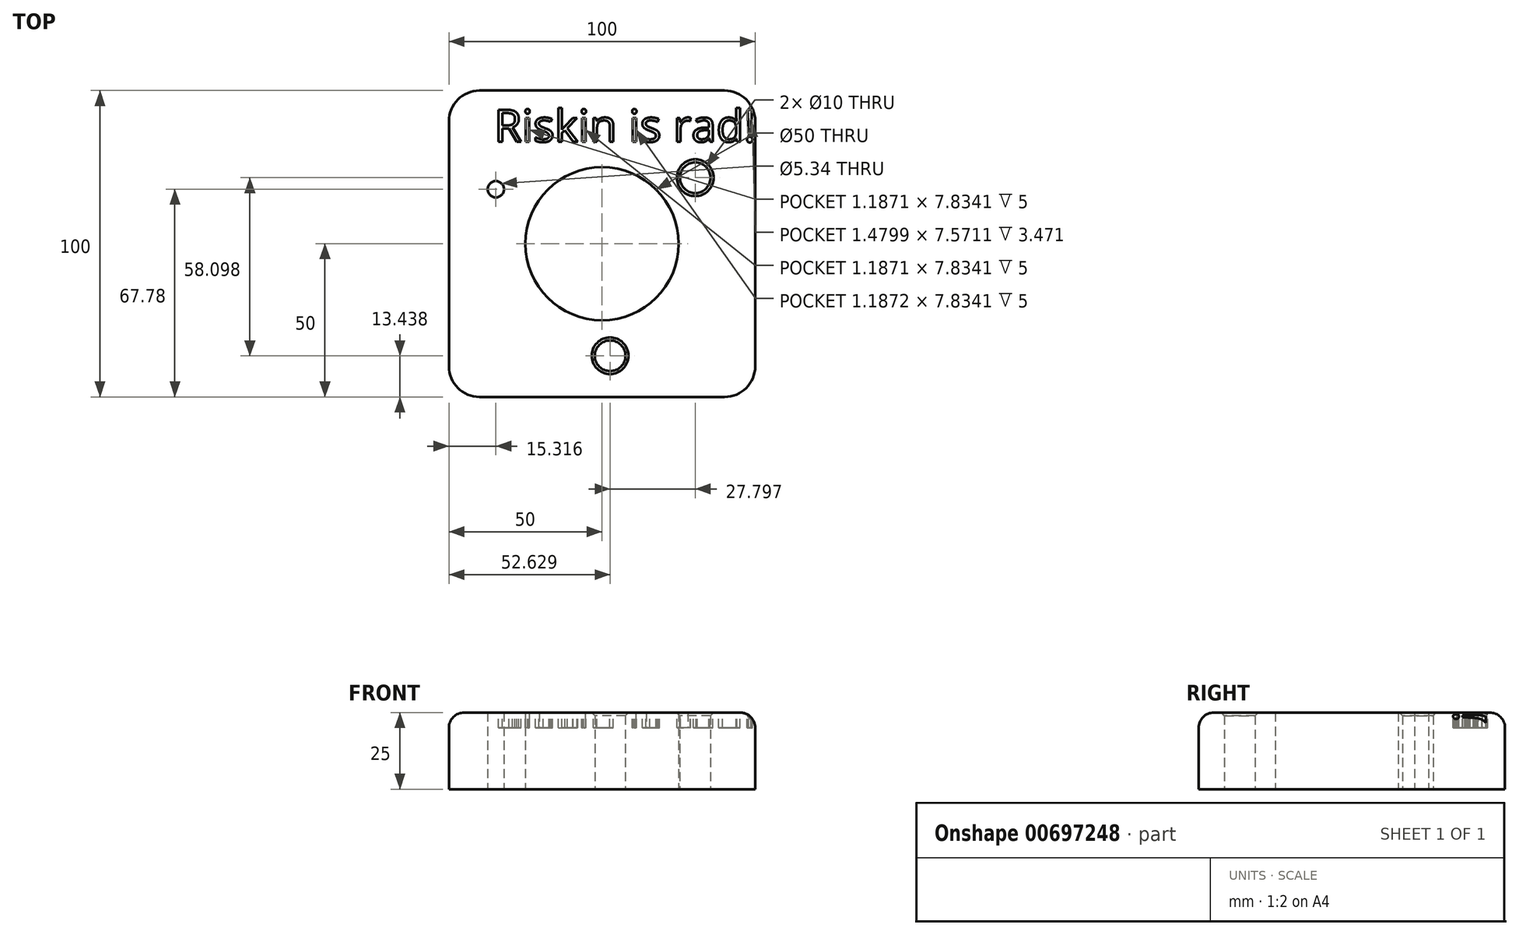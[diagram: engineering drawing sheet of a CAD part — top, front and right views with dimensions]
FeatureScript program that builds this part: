
annotation { "Feature Type Name" : "Feature", "Feature Type Description" : "" }
export const myFeature = defineFeature(function(context is Context, id is Id, definition is map)
    precondition{}
    {
        {
            var Q0;
            Q0=qCreatedBy(makeId("Top.planeOp"),FACE);
            var sketch = newSketch(context, id + "F0", { "sketchPlane" : qUnion([Q0])});
            skCircle(sketch, "E0", {"center": v(0, 0) * mm, "radius": 25 * mm});
            skLineSegment(sketch, "E1.bottom", {"start": v(-40, 50) * mm, "end": v(40, 50) * mm});
            skLineSegment(sketch, "E1.top", {"start": v(-40, -50) * mm, "end": v(40, -50) * mm});
            skLineSegment(sketch, "E1.left", {"start": v(-50, 40) * mm, "end": v(-50, -40) * mm});
            skLineSegment(sketch, "E1.right", {"start": v(50, 40) * mm, "end": v(50, -40) * mm});
            skCircle(sketch, "E2", {"center": v(-34.68, 17.78) * mm, "radius": 5 * mm});
            skCircle(sketch, "E3", {"center": v(2.63, -36.56) * mm, "radius": 5 * mm});
            skCircle(sketch, "E4", {"center": v(30.43, 21.54) * mm, "radius": 5 * mm});
            skPoint(sketch, "E5.visualSharp", {"position": v(-50, 50) * mm});
            skArc(sketch, "E5.filletArc", {"start": v(-40, 50) * mm, "mid": v(-47.07, 47.07) * mm, "end": v(-50, 40) * mm});
            skPoint(sketch, "E6.visualSharp", {"position": v(50, 50) * mm});
            skArc(sketch, "E6.filletArc", {"start": v(50, 40) * mm, "mid": v(47.07, 47.07) * mm, "end": v(40, 50) * mm});
            skPoint(sketch, "E7.visualSharp", {"position": v(50, -50) * mm});
            skArc(sketch, "E7.filletArc", {"start": v(40, -50) * mm, "mid": v(47.07, -47.07) * mm, "end": v(50, -40) * mm});
            skPoint(sketch, "E8.visualSharp", {"position": v(-50, -50) * mm});
            skArc(sketch, "E8.filletArc", {"start": v(-50, -40) * mm, "mid": v(-47.07, -47.07) * mm, "end": v(-40, -50) * mm});
            skCircle(sketch, "E9", {"center": v(-34.68, 17.78) * mm, "radius": 2.67 * mm});
            skSolve(sketch);
        }
        {
            var Q0;
            Q0 = qSketchRegion(id + "F0", true);
            var Q1;
            Q1=makeQuery(id+"F0.imprint","IMPRINT",FACE,{"disambiguationData":[TD([[makeQuery(id+"F0.imprint","IMPRINT",EDGE,{"derivedFrom":sQuery(id+"F0.wireOp",EDGE,"E2")}),1.0]])]});
            extrude(context, id + "F1", {"entities" : qUnion([Q0, Q1]), "endBound" : BoundingType.SYMMETRIC, "depth" : 25 * mm, "offsetDistance" : 25 * mm});
        }
        {
            var Q0;
            Q0=makeQuery(id+"F1.opExtrude","CAP_FACE",FACE,{"disambiguationData":[OSD([sQuery(id+"F0.wireOp",EDGE,"E0"),sQuery(id+"F0.wireOp",EDGE,"E1.bottom"),sQuery(id+"F0.wireOp",EDGE,"E1.top"),sQuery(id+"F0.wireOp",EDGE,"E1.left"),sQuery(id+"F0.wireOp",EDGE,"E1.right"),sQuery(id+"F0.wireOp",EDGE,"E2"),sQuery(id+"F0.wireOp",EDGE,"E3"),sQuery(id+"F0.wireOp",EDGE,"E4"),sQuery(id+"F0.wireOp",EDGE,"E5.filletArc"),sQuery(id+"F0.wireOp",EDGE,"E6.filletArc"),sQuery(id+"F0.wireOp",EDGE,"E7.filletArc"),sQuery(id+"F0.wireOp",EDGE,"E8.filletArc")])],"isStart":false});
            var sketch = newSketch(context, id + "F2", { "sketchPlane" : qUnion([Q0])});
            skText(sketch, "E10", { "text": "Riskin is rad!", "fontName": "OpenSans-Regular.ttf"});
            const initialGuessF2  = {"E10": [-0.03522, 0.03325, 1, 0, 0.01054]};
            skSetInitialGuess(sketch, initialGuessF2);
            skSolve(sketch);
        }
        {
            var Q0;
            Q0 = qSketchRegion(id + "F2", true);
            extrude(context, id + "F3", {"entities" : qUnion([Q0]), "operationType" : NewBodyOperationType.REMOVE, "oppositeDirection" : true, "depth" : 5 * mm, "offsetDistance" : 25 * mm});
        }
        {
            var Q0;
            Q0=makeQuery(id+"F1.opExtrude","CAP_EDGE",EDGE,{"disambiguationData":[OSD([sQuery(id+"F0.wireOp",EDGE,"E1.left")])],"isStart":false});
            fillet(context, id + "F4", {"entities" : qUnion([Q0]), "radius" : 5 * mm, "tangentPropagation" : true, "allowEdgeOverflow" : false});
        }
        {
            var Q0;
            Q0=makeQuery(id+"F1.opExtrude","CAP_EDGE",EDGE,{"disambiguationData":[OSD([sQuery(id+"F0.wireOp",EDGE,"E2")])],"isStart":false});
            var Q1;
            Q1=makeQuery(id+"F1.opExtrude","CAP_EDGE",EDGE,{"disambiguationData":[OSD([sQuery(id+"F0.wireOp",EDGE,"E4")])],"isStart":false});
            var Q2;
            Q2=makeQuery(id+"F1.opExtrude","CAP_EDGE",EDGE,{"disambiguationData":[OSD([sQuery(id+"F0.wireOp",EDGE,"E3")])],"isStart":false});
            chamfer(context, id + "F5", {"entities" : qUnion([Q0, Q1, Q2]), "width" : 1 * mm, "tangentPropagation" : true});
        }
    });
